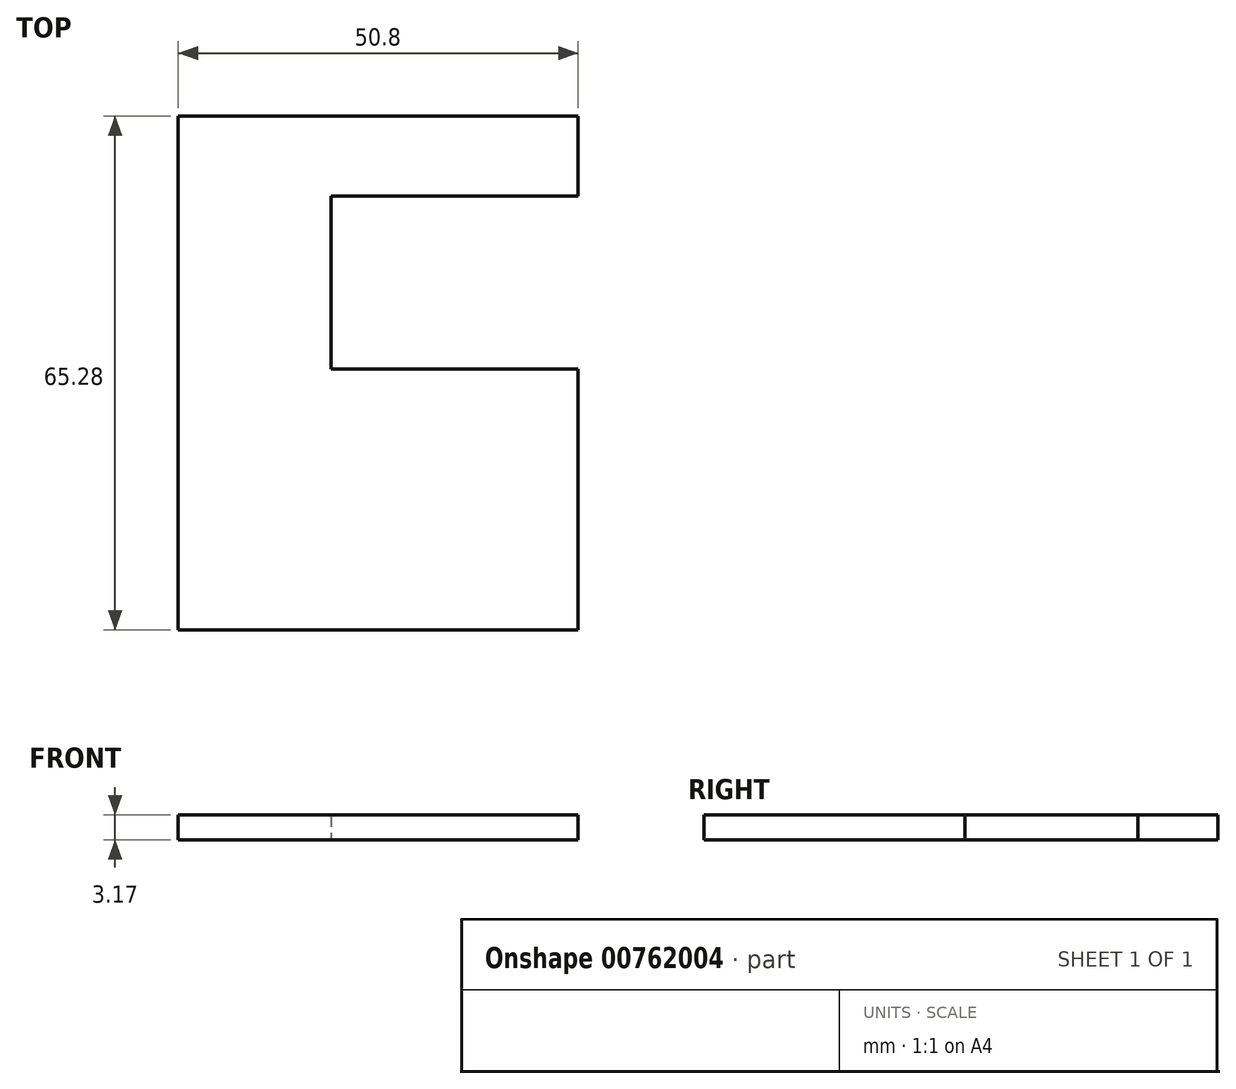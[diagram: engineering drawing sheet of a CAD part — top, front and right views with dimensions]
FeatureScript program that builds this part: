
annotation { "Feature Type Name" : "Feature", "Feature Type Description" : "" }
export const myFeature = defineFeature(function(context is Context, id is Id, definition is map)
    precondition{}
    {
        {
            var Q0;
            Q0=qCreatedBy(makeId("Top.planeOp"),FACE);
            var sketch = newSketch(context, id + "F0", { "sketchPlane" : qUnion([Q0])});
            skLineSegment(sketch, "E0.bottom", {"start": v(-105.75, 18.07) * mm, "end": v(-54.95, 18.07) * mm});
            skLineSegment(sketch, "E0.top", {"start": v(-105.75, -47.2) * mm, "end": v(-54.95, -47.2) * mm});
            skLineSegment(sketch, "E0.left", {"start": v(-105.75, 18.07) * mm, "end": v(-105.75, -47.2) * mm});
            skLineSegment(sketch, "E0.right", {"start": v(-54.95, 18.07) * mm, "end": v(-54.95, 7.9) * mm});
            skPoint(sketch, "E1", {"position": v(-80.35, 18.07) * mm});
            skPoint(sketch, "E2", {"position": v(-54.95, 7.9) * mm});
            skPoint(sketch, "E3", {"position": v(-54.95, -14.1) * mm});
            skPoint(sketch, "E4", {"position": v(-86.35, 18.07) * mm});
            skPoint(sketch, "E5", {"position": v(-74.85, 18.07) * mm});
            skLineSegment(sketch, "E6", {"start": v(-54.95, 7.9) * mm, "end": v(-74.35, 7.9) * mm});
            skLineSegment(sketch, "E7", {"start": v(-54.95, -14.1) * mm, "end": v(-76.43, -14.1) * mm});
            skLineSegment(sketch, "E8", {"start": v(-86.35, 7.9) * mm, "end": v(-86.35, -14.1) * mm});
            skLineSegment(sketch, "E9", {"start": v(-86.35, -14.1) * mm, "end": v(-76.43, -14.1) * mm});
            skLineSegment(sketch, "E10", {"start": v(-74.35, 7.9) * mm, "end": v(-86.35, 7.9) * mm});
            skLineSegment(sketch, "E11.trimOffspring", {"start": v(-54.95, -14.1) * mm, "end": v(-54.95, -47.2) * mm});
            skSolve(sketch);
        }
        {
            var Q0;
            Q0=makeQuery(id+"F0.imprint","IMPRINT",FACE,{"disambiguationData":[TD([[makeQuery(id+"F0.imprint","IMPRINT",EDGE,{"derivedFrom":sQuery(id+"F0.wireOp",EDGE,"E0.bottom")}),-1.0]])]});
            extrude(context, id + "F1", {"entities" : qUnion([Q0]), "depth" : 3.17 * mm, "offsetDistance" : 25.4 * mm});
        }
    });
